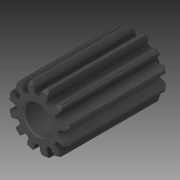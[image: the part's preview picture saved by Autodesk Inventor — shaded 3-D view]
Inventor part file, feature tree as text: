
AUTODESK INVENTOR PART (.ipt)
format: ipt  version: 2019 (Build 230136000, 136)  size: 310,272 bytes
history: native  units: in
note: dims shown in document units (in); Inventor stores cm internally (conversion verified against a paired STEP export)
features: mirror x1
ambient origin geometry x8: Origin, YZ Plane, XZ Plane, XY Plane, X Axis, Y Axis, Z Axis, Center Point
bodies: Solid1 (feature_tree)
feature tree (1):
  mirror  "Mirror1"
